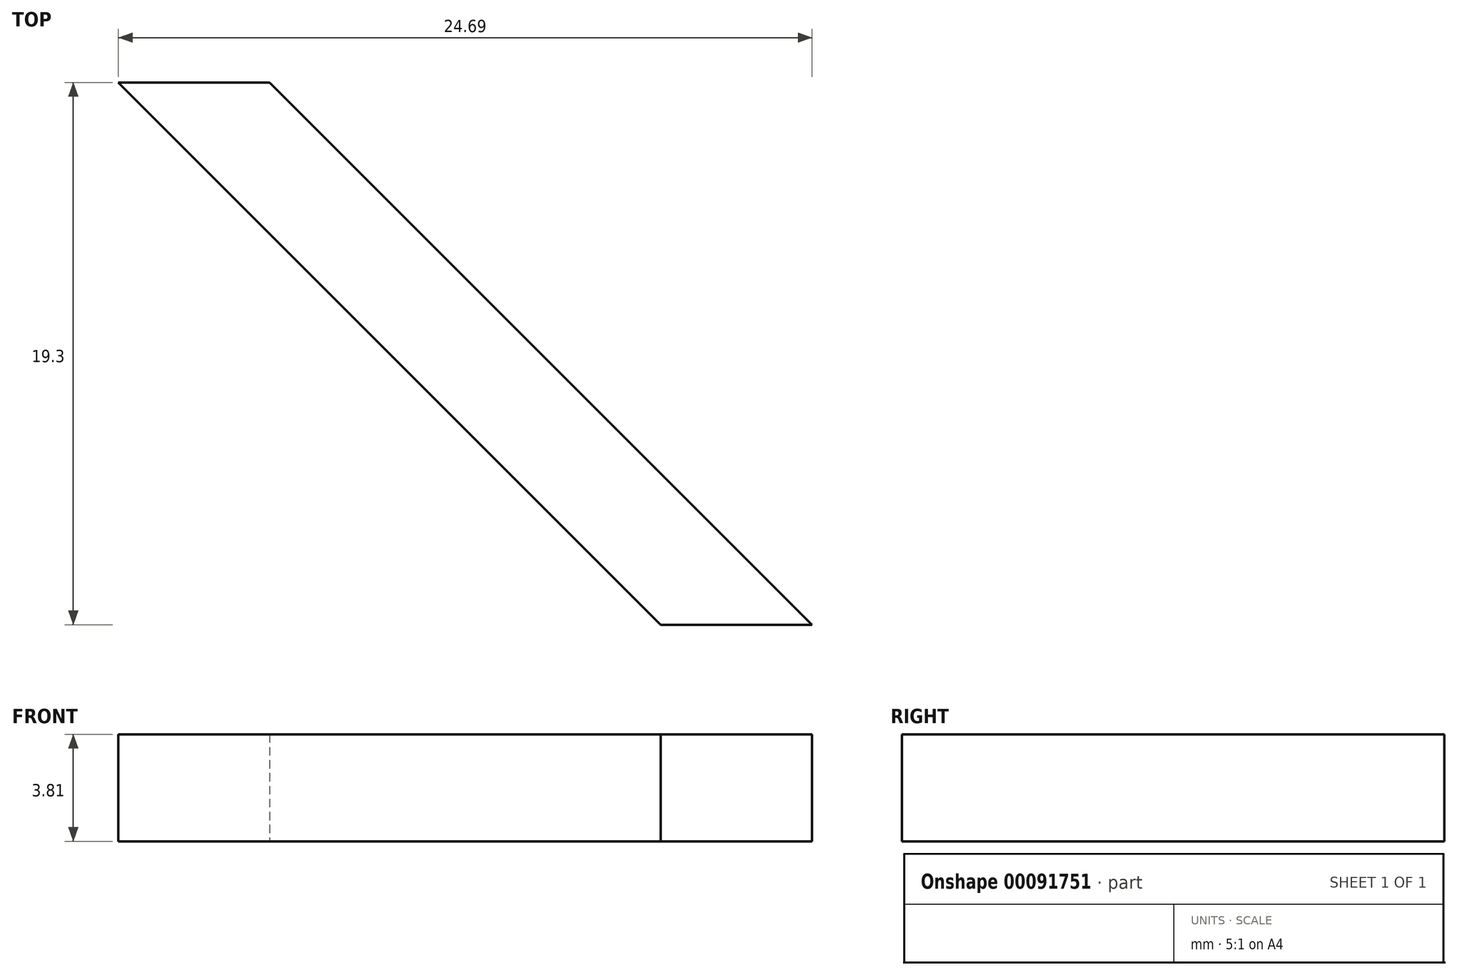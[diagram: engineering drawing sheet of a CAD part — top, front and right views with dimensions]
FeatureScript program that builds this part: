
annotation { "Feature Type Name" : "Feature", "Feature Type Description" : "" }
export const myFeature = defineFeature(function(context is Context, id is Id, definition is map)
    precondition{}
    {
        {
            var Q0;
            Q0=qCreatedBy(makeId("Top.planeOp"),FACE);
            var sketch = newSketch(context, id + "F0", { "sketchPlane" : qUnion([Q0])});
            skLineSegment(sketch, "E0", {"start": v(0, 0) * mm, "end": v(5.39, 0) * mm});
            skLineSegment(sketch, "E1", {"start": v(5.39, 0) * mm, "end": v(24.7, -19.3) * mm});
            skLineSegment(sketch, "E2", {"start": v(0, 0) * mm, "end": v(19.3, -19.3) * mm});
            skLineSegment(sketch, "E3", {"start": v(19.3, -19.3) * mm, "end": v(24.7, -19.3) * mm});
            skSolve(sketch);
        }
        {
            var Q0;
            Q0 = qSketchRegion(id + "F0", true);
            extrude(context, id + "F1", {"entities" : qUnion([Q0]), "depth" : 3.8 * mm});
        }
    });
